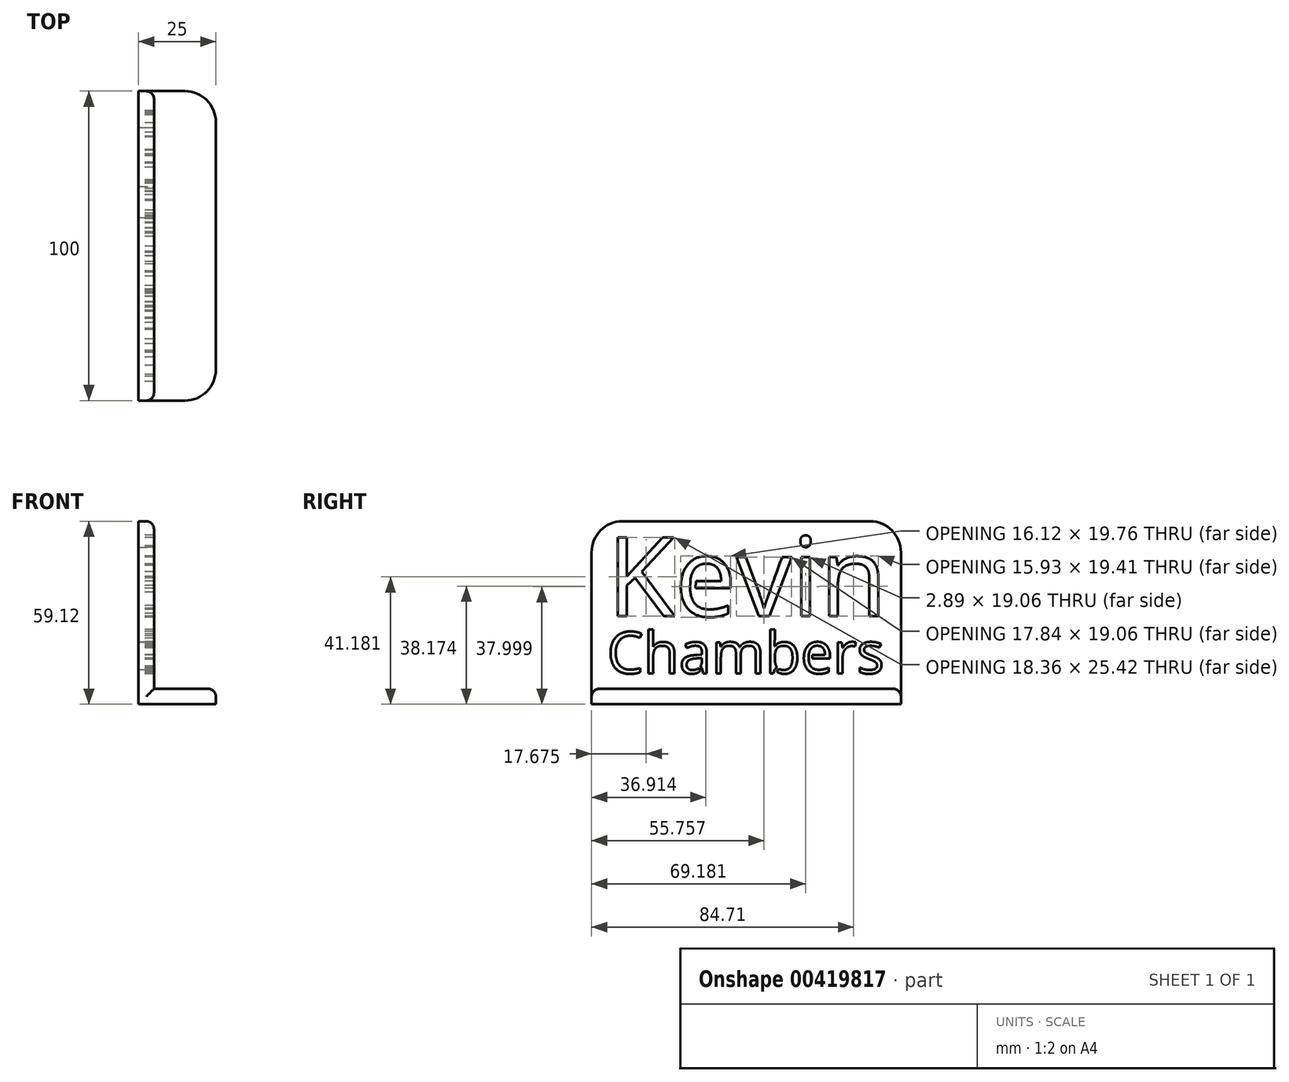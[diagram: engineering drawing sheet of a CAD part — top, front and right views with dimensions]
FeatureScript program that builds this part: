
annotation { "Feature Type Name" : "Feature", "Feature Type Description" : "" }
export const myFeature = defineFeature(function(context is Context, id is Id, definition is map)
    precondition{}
    {
        {
            var Q0;
            Q0=qCreatedBy(makeId("Right.planeOp"),FACE);
            var sketch = newSketch(context, id + "F0", { "sketchPlane" : qUnion([Q0])});
            skLineSegment(sketch, "E0.bottom", {"start": v(0, 0) * mm, "end": v(100, 0) * mm});
            skLineSegment(sketch, "E0.top", {"start": v(0, 54.12) * mm, "end": v(100, 54.12) * mm});
            skLineSegment(sketch, "E0.left", {"start": v(0, 0) * mm, "end": v(0, 54.12) * mm});
            skLineSegment(sketch, "E0.right", {"start": v(100, 0) * mm, "end": v(100, 54.12) * mm});
            skText(sketch, "E1", { "text": "Kevin", "fontName": "OpenSans-Regular.ttf"});
            skText(sketch, "E2", { "text": "Chambers", "fontName": "OpenSans-Regular.ttf"});
            skLineSegment(sketch, "E3", {"start": v(31.97, 34.9) * mm, "end": v(31.85, 32.46) * mm});
            skLineSegment(sketch, "E4", {"start": v(31.85, 32.46) * mm, "end": v(33.67, 32.46) * mm});
            skLineSegment(sketch, "E5", {"start": v(33.67, 32.46) * mm, "end": v(33.71, 34.86) * mm});
            skLineSegment(sketch, "E6", {"start": v(33.71, 34.86) * mm, "end": v(31.97, 34.9) * mm});
            skLineSegment(sketch, "E7", {"start": v(59.2, 6.23) * mm, "end": v(59.89, 7.12) * mm});
            skLineSegment(sketch, "E8", {"start": v(59.89, 7.12) * mm, "end": v(60.67, 6.52) * mm});
            skLineSegment(sketch, "E9", {"start": v(60.67, 6.52) * mm, "end": v(59.78, 5.36) * mm});
            skLineSegment(sketch, "E10", {"start": v(59.78, 5.36) * mm, "end": v(59.2, 6.23) * mm});
            skLineSegment(sketch, "E11", {"start": v(35.74, 6.23) * mm, "end": v(35.23, 7.33) * mm});
            skLineSegment(sketch, "E12", {"start": v(35.23, 7.33) * mm, "end": v(34.64, 6.8) * mm});
            skLineSegment(sketch, "E13", {"start": v(34.64, 6.8) * mm, "end": v(35.27, 5.44) * mm});
            skLineSegment(sketch, "E14", {"start": v(35.27, 5.44) * mm, "end": v(35.74, 6.23) * mm});
            skLineSegment(sketch, "E15", {"start": v(70.25, 9.58) * mm, "end": v(70.25, 11.07) * mm});
            skLineSegment(sketch, "E16", {"start": v(70.25, 11.07) * mm, "end": v(71.3, 11.07) * mm});
            skLineSegment(sketch, "E17", {"start": v(71.3, 11.07) * mm, "end": v(71.3, 9.2) * mm});
            skLineSegment(sketch, "E18", {"start": v(71.3, 9.2) * mm, "end": v(70.25, 9.58) * mm});
            const initialGuessF0  = {"E1": [0.005, 0.02347, 1, 0, 0.02564], "E2": [0.005, 0.005, 1, 0, 0.01347]};
            skSetInitialGuess(sketch, initialGuessF0);
            skSolve(sketch);
        }
        {
            var Q0;
            Q0=makeQuery(id+"F0.imprint","IMPRINT",FACE,{"disambiguationData":[TD([[makeQuery(id+"F0.imprint","IMPRINT",EDGE,{"derivedFrom":sQuery(id+"F0.wireOp",EDGE,"E2.sketch_text.stroke-103")}),1.0]])]});
            var Q1;
            Q1=makeQuery(id+"F0.imprint","IMPRINT",FACE,{"disambiguationData":[TD([[makeQuery(id+"F0.imprint","IMPRINT",EDGE,{"derivedFrom":sQuery(id+"F0.wireOp",EDGE,"E2.sketch_text.stroke-125")}),1.0]])]});
            var Q2;
            {var subQ0=sQuery(id+"F0.wireOp",EDGE,"E17");var subQ1=sQuery(id+"F0.wireOp",EDGE,"E2.sketch_text.stroke-118");var subQ2=makeQuery(id+"F0.imprint","INTERSECT",VERTEX,{"derivedFrom":[subQ1,subQ0]});Q2=makeQuery(id+"F0.imprint","IMPRINT",FACE,{"disambiguationData":[TD([[makeQuery(id+"F0.imprint","IMPRINT",EDGE,{"disambiguationData":[TD([[subQ2,-1.0]])],"derivedFrom":subQ1}),-1.0]])]});}
            var Q3;
            Q3=makeQuery(id+"F0.imprint","IMPRINT",FACE,{"disambiguationData":[TD([[makeQuery(id+"F0.imprint","IMPRINT",EDGE,{"derivedFrom":sQuery(id+"F0.wireOp",EDGE,"E0.bottom")}),1.0]])]});
            var Q4;
            {var subQ1=sQuery(id+"F0.wireOp",EDGE,"E2.sketch_text.stroke-93");var subQ7=sQuery(id+"F0.wireOp",EDGE,"E9");var subQ9=makeQuery(id+"F0.imprint","INTERSECT",VERTEX,{"derivedFrom":[subQ1,subQ7]});Q4=makeQuery(id+"F0.imprint","IMPRINT",FACE,{"disambiguationData":[TD([[makeQuery(id+"F0.imprint","IMPRINT",EDGE,{"disambiguationData":[TD([[subQ9,-1.0]])],"derivedFrom":subQ1}),-1.0]])]});}
            var Q5;
            {var subQ5=sQuery(id+"F0.wireOp",EDGE,"E18");Q5=makeQuery(id+"F0.imprint","IMPRINT",FACE,{"disambiguationData":[TD([[makeQuery(id+"F0.imprint","IMPRINT",EDGE,{"derivedFrom":subQ5}),-1.0]])]});}
            var Q6;
            {var subQ5=sQuery(id+"F0.wireOp",EDGE,"E16");Q6=makeQuery(id+"F0.imprint","IMPRINT",FACE,{"disambiguationData":[TD([[makeQuery(id+"F0.imprint","IMPRINT",EDGE,{"derivedFrom":subQ5}),-1.0]])]});}
            var Q7;
            {var subQ5=sQuery(id+"F0.wireOp",EDGE,"E10");Q7=makeQuery(id+"F0.imprint","IMPRINT",FACE,{"disambiguationData":[TD([[makeQuery(id+"F0.imprint","IMPRINT",EDGE,{"derivedFrom":subQ5}),-1.0]])]});}
            var Q8;
            {var subQ0=sQuery(id+"F0.wireOp",EDGE,"E8");Q8=makeQuery(id+"F0.imprint","IMPRINT",FACE,{"disambiguationData":[TD([[makeQuery(id+"F0.imprint","IMPRINT",EDGE,{"derivedFrom":subQ0}),-1.0]])]});}
            var Q9;
            {var subQ8=sQuery(id+"F0.wireOp",EDGE,"E2.sketch_text.stroke-54");Q9=makeQuery(id+"F0.imprint","IMPRINT",FACE,{"disambiguationData":[TD([[makeQuery(id+"F0.imprint","IMPRINT",EDGE,{"derivedFrom":subQ8}),1.0]])]});}
            var Q10;
            {var subQ0=sQuery(id+"F0.wireOp",EDGE,"E11");var subQ1=sQuery(id+"F0.wireOp",EDGE,"E2.sketch_text.stroke-35");var subQ2=makeQuery(id+"F0.imprint","INTERSECT",VERTEX,{"derivedFrom":[subQ1,subQ0]});Q10=makeQuery(id+"F0.imprint","IMPRINT",FACE,{"disambiguationData":[TD([[makeQuery(id+"F0.imprint","IMPRINT",EDGE,{"disambiguationData":[TD([[subQ2,-1.0]])],"derivedFrom":subQ1}),-1.0]])]});}
            var Q11;
            {var subQ5=sQuery(id+"F0.wireOp",EDGE,"E14");Q11=makeQuery(id+"F0.imprint","IMPRINT",FACE,{"disambiguationData":[TD([[makeQuery(id+"F0.imprint","IMPRINT",EDGE,{"derivedFrom":subQ5}),1.0]])]});}
            var Q12;
            {var subQ0=sQuery(id+"F0.wireOp",EDGE,"E12");Q12=makeQuery(id+"F0.imprint","IMPRINT",FACE,{"disambiguationData":[TD([[makeQuery(id+"F0.imprint","IMPRINT",EDGE,{"derivedFrom":subQ0}),1.0]])]});}
            var Q13;
            {var subQ0=sQuery(id+"F0.wireOp",EDGE,"E5");var subQ1=sQuery(id+"F0.wireOp",EDGE,"E1.sketch_text.stroke-19");var subQ2=makeQuery(id+"F0.imprint","INTERSECT",VERTEX,{"derivedFrom":[subQ1,subQ0]});Q13=makeQuery(id+"F0.imprint","IMPRINT",FACE,{"disambiguationData":[TD([[makeQuery(id+"F0.imprint","IMPRINT",EDGE,{"disambiguationData":[TD([[subQ2,-1.0]])],"derivedFrom":subQ1}),-1.0]])]});}
            var Q14;
            Q14=makeQuery(id+"F0.imprint","IMPRINT",FACE,{"disambiguationData":[TD([[makeQuery(id+"F0.imprint","IMPRINT",EDGE,{"derivedFrom":sQuery(id+"F0.wireOp",EDGE,"E1.sketch_text.stroke-26")}),1.0]])]});
            var Q15;
            {var subQ5=sQuery(id+"F0.wireOp",EDGE,"E6");Q15=makeQuery(id+"F0.imprint","IMPRINT",FACE,{"disambiguationData":[TD([[makeQuery(id+"F0.imprint","IMPRINT",EDGE,{"derivedFrom":subQ5}),1.0]])]});}
            var Q16;
            {var subQ5=sQuery(id+"F0.wireOp",EDGE,"E4");Q16=makeQuery(id+"F0.imprint","IMPRINT",FACE,{"disambiguationData":[TD([[makeQuery(id+"F0.imprint","IMPRINT",EDGE,{"derivedFrom":subQ5}),1.0]])]});}
            extrude(context, id + "F1", {"entities" : qUnion([Q0, Q1, Q2, Q3, Q4, Q5, Q6, Q7, Q8, Q9, Q10, Q11, Q12, Q13, Q14, Q15, Q16]), "depth" : 5 * mm});
        }
        {
            var Q0;
            Q0=makeQuery(id+"F1.opExtrude","SWEPT_EDGE",EDGE,{"disambiguationData":[OSD([sQuery(id+"F0.wireOp",EDGE,"E0.top"),sQuery(id+"F0.wireOp",EDGE,"E0.right")])]});
            var Q1;
            Q1=makeQuery(id+"F1.opExtrude","SWEPT_EDGE",EDGE,{"disambiguationData":[OSD([sQuery(id+"F0.wireOp",EDGE,"E0.top"),sQuery(id+"F0.wireOp",EDGE,"E0.left")])]});
            fillet(context, id + "F2", {"entities" : qUnion([Q0, Q1]), "radius" : 10 * mm, "tangentPropagation" : true, "allowEdgeOverflow" : false});
        }
        {
            var Q0;
            Q0=makeQuery(id+"F1.opExtrude","SWEPT_FACE",FACE,{"disambiguationData":[OSD([sQuery(id+"F0.wireOp",EDGE,"E0.bottom")])]});
            var sketch = newSketch(context, id + "F3", { "sketchPlane" : qUnion([Q0])});
            skLineSegment(sketch, "E19.bottom", {"start": v(0, 0) * mm, "end": v(25, 0) * mm});
            skLineSegment(sketch, "E19.top", {"start": v(0, -100) * mm, "end": v(25, -100) * mm});
            skLineSegment(sketch, "E19.left", {"start": v(0, 0) * mm, "end": v(0, -100) * mm});
            skLineSegment(sketch, "E19.right", {"start": v(25, 0) * mm, "end": v(25, -100) * mm});
            skSolve(sketch);
        }
        {
            var Q0;
            Q0 = qSketchRegion(id + "F3", true);
            extrude(context, id + "F4", {"entities" : qUnion([Q0]), "operationType" : NewBodyOperationType.ADD, "depth" : 5 * mm});
        }
        {
            var Q0;
            Q0=makeQuery(id+"F4.opExtrude","SWEPT_EDGE",EDGE,{"disambiguationData":[OSD([sQuery(id+"F3.wireOp",EDGE,"E19.bottom"),sQuery(id+"F3.wireOp",EDGE,"E19.right")])]});
            var Q1;
            Q1=makeQuery(id+"F4.opExtrude","SWEPT_EDGE",EDGE,{"disambiguationData":[OSD([sQuery(id+"F3.wireOp",EDGE,"E19.top"),sQuery(id+"F3.wireOp",EDGE,"E19.right")])]});
            fillet(context, id + "F5", {"entities" : qUnion([Q0, Q1]), "radius" : 10 * mm, "tangentPropagation" : true, "allowEdgeOverflow" : false});
        }
        {
            var Q0;
            {var subQ0=sQuery(id+"F0.wireOp",EDGE,"E0.left");var subQ1=sQuery(id+"F0.wireOp",EDGE,"E0.top");Q0=makeQuery(id+"F2.opFillet","BLEND_EDGE",EDGE,{"blendedFrom":[makeQuery(id+"F1.opExtrude","SWEPT_EDGE",EDGE,{"disambiguationData":[OSD([subQ1,subQ0])]}),makeQuery(id+"F1.opExtrude","CAP_FACE",FACE,{"disambiguationData":[OSD([sQuery(id+"F0.wireOp",EDGE,"E0.bottom"),subQ1,subQ0,sQuery(id+"F0.wireOp",EDGE,"E0.right"),sQuery(id+"F0.wireOp",EDGE,"E1.sketch_text.stroke-0"),sQuery(id+"F0.wireOp",EDGE,"E1.sketch_text.stroke-1"),sQuery(id+"F0.wireOp",EDGE,"E1.sketch_text.stroke-2"),sQuery(id+"F0.wireOp",EDGE,"E1.sketch_text.stroke-3"),sQuery(id+"F0.wireOp",EDGE,"E1.sketch_text.stroke-4"),sQuery(id+"F0.wireOp",EDGE,"E1.sketch_text.stroke-5"),sQuery(id+"F0.wireOp",EDGE,"E1.sketch_text.stroke-6"),sQuery(id+"F0.wireOp",EDGE,"E1.sketch_text.stroke-7"),sQuery(id+"F0.wireOp",EDGE,"E1.sketch_text.stroke-8"),sQuery(id+"F0.wireOp",EDGE,"E1.sketch_text.stroke-9"),sQuery(id+"F0.wireOp",EDGE,"E1.sketch_text.stroke-10"),sQuery(id+"F0.wireOp",EDGE,"E1.sketch_text.stroke-11"),sQuery(id+"F0.wireOp",EDGE,"E1.sketch_text.stroke-12"),sQuery(id+"F0.wireOp",EDGE,"E1.sketch_text.stroke-13"),sQuery(id+"F0.wireOp",EDGE,"E1.sketch_text.stroke-14"),sQuery(id+"F0.wireOp",EDGE,"E1.sketch_text.stroke-15"),sQuery(id+"F0.wireOp",EDGE,"E1.sketch_text.stroke-16"),sQuery(id+"F0.wireOp",EDGE,"E1.sketch_text.stroke-17"),sQuery(id+"F0.wireOp",EDGE,"E1.sketch_text.stroke-18"),sQuery(id+"F0.wireOp",EDGE,"E1.sketch_text.stroke-19"),sQuery(id+"F0.wireOp",EDGE,"E1.sketch_text.stroke-20"),sQuery(id+"F0.wireOp",EDGE,"E1.sketch_text.stroke-21"),sQuery(id+"F0.wireOp",EDGE,"E1.sketch_text.stroke-22"),sQuery(id+"F0.wireOp",EDGE,"E1.sketch_text.stroke-23"),sQuery(id+"F0.wireOp",EDGE,"E1.sketch_text.stroke-24"),sQuery(id+"F0.wireOp",EDGE,"E1.sketch_text.stroke-25"),sQuery(id+"F0.wireOp",EDGE,"E1.sketch_text.stroke-26"),sQuery(id+"F0.wireOp",EDGE,"E1.sketch_text.stroke-27"),sQuery(id+"F0.wireOp",EDGE,"E1.sketch_text.stroke-28"),sQuery(id+"F0.wireOp",EDGE,"E1.sketch_text.stroke-29"),sQuery(id+"F0.wireOp",EDGE,"E1.sketch_text.stroke-30"),sQuery(id+"F0.wireOp",EDGE,"E1.sketch_text.stroke-31"),sQuery(id+"F0.wireOp",EDGE,"E1.sketch_text.stroke-32"),sQuery(id+"F0.wireOp",EDGE,"E1.sketch_text.stroke-33"),sQuery(id+"F0.wireOp",EDGE,"E1.sketch_text.stroke-34"),sQuery(id+"F0.wireOp",EDGE,"E1.sketch_text.stroke-35"),sQuery(id+"F0.wireOp",EDGE,"E1.sketch_text.stroke-36"),sQuery(id+"F0.wireOp",EDGE,"E1.sketch_text.stroke-37"),sQuery(id+"F0.wireOp",EDGE,"E1.sketch_text.stroke-38"),sQuery(id+"F0.wireOp",EDGE,"E1.sketch_text.stroke-39"),sQuery(id+"F0.wireOp",EDGE,"E1.sketch_text.stroke-40"),sQuery(id+"F0.wireOp",EDGE,"E1.sketch_text.stroke-41"),sQuery(id+"F0.wireOp",EDGE,"E1.sketch_text.stroke-42"),sQuery(id+"F0.wireOp",EDGE,"E1.sketch_text.stroke-43"),sQuery(id+"F0.wireOp",EDGE,"E1.sketch_text.stroke-44"),sQuery(id+"F0.wireOp",EDGE,"E1.sketch_text.stroke-45"),sQuery(id+"F0.wireOp",EDGE,"E1.sketch_text.stroke-46"),sQuery(id+"F0.wireOp",EDGE,"E1.sketch_text.stroke-47"),sQuery(id+"F0.wireOp",EDGE,"E1.sketch_text.stroke-48"),sQuery(id+"F0.wireOp",EDGE,"E1.sketch_text.stroke-49"),sQuery(id+"F0.wireOp",EDGE,"E1.sketch_text.stroke-50"),sQuery(id+"F0.wireOp",EDGE,"E1.sketch_text.stroke-51"),sQuery(id+"F0.wireOp",EDGE,"E1.sketch_text.stroke-52"),sQuery(id+"F0.wireOp",EDGE,"E1.sketch_text.stroke-53"),sQuery(id+"F0.wireOp",EDGE,"E1.sketch_text.stroke-54"),sQuery(id+"F0.wireOp",EDGE,"E1.sketch_text.stroke-55"),sQuery(id+"F0.wireOp",EDGE,"E1.sketch_text.stroke-56"),sQuery(id+"F0.wireOp",EDGE,"E1.sketch_text.stroke-57"),sQuery(id+"F0.wireOp",EDGE,"E1.sketch_text.stroke-58"),sQuery(id+"F0.wireOp",EDGE,"E1.sketch_text.stroke-59"),sQuery(id+"F0.wireOp",EDGE,"E1.sketch_text.stroke-60"),sQuery(id+"F0.wireOp",EDGE,"E1.sketch_text.stroke-61"),sQuery(id+"F0.wireOp",EDGE,"E1.sketch_text.stroke-62"),sQuery(id+"F0.wireOp",EDGE,"E1.sketch_text.stroke-63"),sQuery(id+"F0.wireOp",EDGE,"E1.sketch_text.stroke-64"),sQuery(id+"F0.wireOp",EDGE,"E1.sketch_text.stroke-65"),sQuery(id+"F0.wireOp",EDGE,"E1.sketch_text.stroke-66"),sQuery(id+"F0.wireOp",EDGE,"E1.sketch_text.stroke-67"),sQuery(id+"F0.wireOp",EDGE,"E1.sketch_text.stroke-68"),sQuery(id+"F0.wireOp",EDGE,"E1.sketch_text.stroke-69"),sQuery(id+"F0.wireOp",EDGE,"E2.sketch_text.stroke-0"),sQuery(id+"F0.wireOp",EDGE,"E2.sketch_text.stroke-1"),sQuery(id+"F0.wireOp",EDGE,"E2.sketch_text.stroke-2"),sQuery(id+"F0.wireOp",EDGE,"E2.sketch_text.stroke-3"),sQuery(id+"F0.wireOp",EDGE,"E2.sketch_text.stroke-4"),sQuery(id+"F0.wireOp",EDGE,"E2.sketch_text.stroke-5"),sQuery(id+"F0.wireOp",EDGE,"E2.sketch_text.stroke-6"),sQuery(id+"F0.wireOp",EDGE,"E2.sketch_text.stroke-7"),sQuery(id+"F0.wireOp",EDGE,"E2.sketch_text.stroke-8"),sQuery(id+"F0.wireOp",EDGE,"E2.sketch_text.stroke-9"),sQuery(id+"F0.wireOp",EDGE,"E2.sketch_text.stroke-10"),sQuery(id+"F0.wireOp",EDGE,"E2.sketch_text.stroke-11"),sQuery(id+"F0.wireOp",EDGE,"E2.sketch_text.stroke-12"),sQuery(id+"F0.wireOp",EDGE,"E2.sketch_text.stroke-13"),sQuery(id+"F0.wireOp",EDGE,"E2.sketch_text.stroke-14"),sQuery(id+"F0.wireOp",EDGE,"E2.sketch_text.stroke-15"),sQuery(id+"F0.wireOp",EDGE,"E2.sketch_text.stroke-16"),sQuery(id+"F0.wireOp",EDGE,"E2.sketch_text.stroke-17"),sQuery(id+"F0.wireOp",EDGE,"E2.sketch_text.stroke-18"),sQuery(id+"F0.wireOp",EDGE,"E2.sketch_text.stroke-19"),sQuery(id+"F0.wireOp",EDGE,"E2.sketch_text.stroke-20"),sQuery(id+"F0.wireOp",EDGE,"E2.sketch_text.stroke-21"),sQuery(id+"F0.wireOp",EDGE,"E2.sketch_text.stroke-22"),sQuery(id+"F0.wireOp",EDGE,"E2.sketch_text.stroke-23"),sQuery(id+"F0.wireOp",EDGE,"E2.sketch_text.stroke-24"),sQuery(id+"F0.wireOp",EDGE,"E2.sketch_text.stroke-25"),sQuery(id+"F0.wireOp",EDGE,"E2.sketch_text.stroke-26"),sQuery(id+"F0.wireOp",EDGE,"E2.sketch_text.stroke-27"),sQuery(id+"F0.wireOp",EDGE,"E2.sketch_text.stroke-28"),sQuery(id+"F0.wireOp",EDGE,"E2.sketch_text.stroke-29"),sQuery(id+"F0.wireOp",EDGE,"E2.sketch_text.stroke-30"),sQuery(id+"F0.wireOp",EDGE,"E2.sketch_text.stroke-31"),sQuery(id+"F0.wireOp",EDGE,"E2.sketch_text.stroke-32"),sQuery(id+"F0.wireOp",EDGE,"E2.sketch_text.stroke-33"),sQuery(id+"F0.wireOp",EDGE,"E2.sketch_text.stroke-34"),sQuery(id+"F0.wireOp",EDGE,"E2.sketch_text.stroke-35"),sQuery(id+"F0.wireOp",EDGE,"E2.sketch_text.stroke-36"),sQuery(id+"F0.wireOp",EDGE,"E2.sketch_text.stroke-37"),sQuery(id+"F0.wireOp",EDGE,"E2.sketch_text.stroke-38"),sQuery(id+"F0.wireOp",EDGE,"E2.sketch_text.stroke-39"),sQuery(id+"F0.wireOp",EDGE,"E2.sketch_text.stroke-40"),sQuery(id+"F0.wireOp",EDGE,"E2.sketch_text.stroke-41"),sQuery(id+"F0.wireOp",EDGE,"E2.sketch_text.stroke-42"),sQuery(id+"F0.wireOp",EDGE,"E2.sketch_text.stroke-43"),sQuery(id+"F0.wireOp",EDGE,"E2.sketch_text.stroke-44"),sQuery(id+"F0.wireOp",EDGE,"E2.sketch_text.stroke-45"),sQuery(id+"F0.wireOp",EDGE,"E2.sketch_text.stroke-46"),sQuery(id+"F0.wireOp",EDGE,"E2.sketch_text.stroke-47"),sQuery(id+"F0.wireOp",EDGE,"E2.sketch_text.stroke-48"),sQuery(id+"F0.wireOp",EDGE,"E2.sketch_text.stroke-49"),sQuery(id+"F0.wireOp",EDGE,"E2.sketch_text.stroke-50"),sQuery(id+"F0.wireOp",EDGE,"E2.sketch_text.stroke-51"),sQuery(id+"F0.wireOp",EDGE,"E2.sketch_text.stroke-52"),sQuery(id+"F0.wireOp",EDGE,"E2.sketch_text.stroke-53"),sQuery(id+"F0.wireOp",EDGE,"E2.sketch_text.stroke-54"),sQuery(id+"F0.wireOp",EDGE,"E2.sketch_text.stroke-55"),sQuery(id+"F0.wireOp",EDGE,"E2.sketch_text.stroke-56"),sQuery(id+"F0.wireOp",EDGE,"E2.sketch_text.stroke-57"),sQuery(id+"F0.wireOp",EDGE,"E2.sketch_text.stroke-58"),sQuery(id+"F0.wireOp",EDGE,"E2.sketch_text.stroke-59"),sQuery(id+"F0.wireOp",EDGE,"E2.sketch_text.stroke-60"),sQuery(id+"F0.wireOp",EDGE,"E2.sketch_text.stroke-61"),sQuery(id+"F0.wireOp",EDGE,"E2.sketch_text.stroke-62"),sQuery(id+"F0.wireOp",EDGE,"E2.sketch_text.stroke-63"),sQuery(id+"F0.wireOp",EDGE,"E2.sketch_text.stroke-64"),sQuery(id+"F0.wireOp",EDGE,"E2.sketch_text.stroke-65"),sQuery(id+"F0.wireOp",EDGE,"E2.sketch_text.stroke-66"),sQuery(id+"F0.wireOp",EDGE,"E2.sketch_text.stroke-67"),sQuery(id+"F0.wireOp",EDGE,"E2.sketch_text.stroke-68"),sQuery(id+"F0.wireOp",EDGE,"E2.sketch_text.stroke-69"),sQuery(id+"F0.wireOp",EDGE,"E2.sketch_text.stroke-70"),sQuery(id+"F0.wireOp",EDGE,"E2.sketch_text.stroke-71"),sQuery(id+"F0.wireOp",EDGE,"E2.sketch_text.stroke-72"),sQuery(id+"F0.wireOp",EDGE,"E2.sketch_text.stroke-73"),sQuery(id+"F0.wireOp",EDGE,"E2.sketch_text.stroke-74"),sQuery(id+"F0.wireOp",EDGE,"E2.sketch_text.stroke-75"),sQuery(id+"F0.wireOp",EDGE,"E2.sketch_text.stroke-76"),sQuery(id+"F0.wireOp",EDGE,"E2.sketch_text.stroke-77"),sQuery(id+"F0.wireOp",EDGE,"E2.sketch_text.stroke-78"),sQuery(id+"F0.wireOp",EDGE,"E2.sketch_text.stroke-79"),sQuery(id+"F0.wireOp",EDGE,"E2.sketch_text.stroke-80"),sQuery(id+"F0.wireOp",EDGE,"E2.sketch_text.stroke-81"),sQuery(id+"F0.wireOp",EDGE,"E2.sketch_text.stroke-82"),sQuery(id+"F0.wireOp",EDGE,"E2.sketch_text.stroke-83"),sQuery(id+"F0.wireOp",EDGE,"E2.sketch_text.stroke-84"),sQuery(id+"F0.wireOp",EDGE,"E2.sketch_text.stroke-85"),sQuery(id+"F0.wireOp",EDGE,"E2.sketch_text.stroke-86"),sQuery(id+"F0.wireOp",EDGE,"E2.sketch_text.stroke-87"),sQuery(id+"F0.wireOp",EDGE,"E2.sketch_text.stroke-88"),sQuery(id+"F0.wireOp",EDGE,"E2.sketch_text.stroke-89"),sQuery(id+"F0.wireOp",EDGE,"E2.sketch_text.stroke-90"),sQuery(id+"F0.wireOp",EDGE,"E2.sketch_text.stroke-91"),sQuery(id+"F0.wireOp",EDGE,"E2.sketch_text.stroke-92"),sQuery(id+"F0.wireOp",EDGE,"E2.sketch_text.stroke-93"),sQuery(id+"F0.wireOp",EDGE,"E2.sketch_text.stroke-94"),sQuery(id+"F0.wireOp",EDGE,"E2.sketch_text.stroke-95"),sQuery(id+"F0.wireOp",EDGE,"E2.sketch_text.stroke-96"),sQuery(id+"F0.wireOp",EDGE,"E2.sketch_text.stroke-97"),sQuery(id+"F0.wireOp",EDGE,"E2.sketch_text.stroke-98"),sQuery(id+"F0.wireOp",EDGE,"E2.sketch_text.stroke-99"),sQuery(id+"F0.wireOp",EDGE,"E2.sketch_text.stroke-100"),sQuery(id+"F0.wireOp",EDGE,"E2.sketch_text.stroke-101"),sQuery(id+"F0.wireOp",EDGE,"E2.sketch_text.stroke-102"),sQuery(id+"F0.wireOp",EDGE,"E2.sketch_text.stroke-103"),sQuery(id+"F0.wireOp",EDGE,"E2.sketch_text.stroke-104"),sQuery(id+"F0.wireOp",EDGE,"E2.sketch_text.stroke-105"),sQuery(id+"F0.wireOp",EDGE,"E2.sketch_text.stroke-106"),sQuery(id+"F0.wireOp",EDGE,"E2.sketch_text.stroke-107"),sQuery(id+"F0.wireOp",EDGE,"E2.sketch_text.stroke-108"),sQuery(id+"F0.wireOp",EDGE,"E2.sketch_text.stroke-109"),sQuery(id+"F0.wireOp",EDGE,"E2.sketch_text.stroke-110"),sQuery(id+"F0.wireOp",EDGE,"E2.sketch_text.stroke-111"),sQuery(id+"F0.wireOp",EDGE,"E2.sketch_text.stroke-112"),sQuery(id+"F0.wireOp",EDGE,"E2.sketch_text.stroke-113"),sQuery(id+"F0.wireOp",EDGE,"E2.sketch_text.stroke-114"),sQuery(id+"F0.wireOp",EDGE,"E2.sketch_text.stroke-115"),sQuery(id+"F0.wireOp",EDGE,"E2.sketch_text.stroke-116"),sQuery(id+"F0.wireOp",EDGE,"E2.sketch_text.stroke-117"),sQuery(id+"F0.wireOp",EDGE,"E2.sketch_text.stroke-118"),sQuery(id+"F0.wireOp",EDGE,"E2.sketch_text.stroke-119"),sQuery(id+"F0.wireOp",EDGE,"E2.sketch_text.stroke-120"),sQuery(id+"F0.wireOp",EDGE,"E2.sketch_text.stroke-121"),sQuery(id+"F0.wireOp",EDGE,"E2.sketch_text.stroke-122"),sQuery(id+"F0.wireOp",EDGE,"E2.sketch_text.stroke-123"),sQuery(id+"F0.wireOp",EDGE,"E2.sketch_text.stroke-124"),sQuery(id+"F0.wireOp",EDGE,"E2.sketch_text.stroke-125"),sQuery(id+"F0.wireOp",EDGE,"E2.sketch_text.stroke-126"),sQuery(id+"F0.wireOp",EDGE,"E2.sketch_text.stroke-127"),sQuery(id+"F0.wireOp",EDGE,"E2.sketch_text.stroke-128"),sQuery(id+"F0.wireOp",EDGE,"E2.sketch_text.stroke-129"),sQuery(id+"F0.wireOp",EDGE,"E2.sketch_text.stroke-130"),sQuery(id+"F0.wireOp",EDGE,"E2.sketch_text.stroke-131"),sQuery(id+"F0.wireOp",EDGE,"E2.sketch_text.stroke-132"),sQuery(id+"F0.wireOp",EDGE,"E2.sketch_text.stroke-133"),sQuery(id+"F0.wireOp",EDGE,"E2.sketch_text.stroke-134"),sQuery(id+"F0.wireOp",EDGE,"E2.sketch_text.stroke-135"),sQuery(id+"F0.wireOp",EDGE,"E2.sketch_text.stroke-136"),sQuery(id+"F0.wireOp",EDGE,"E2.sketch_text.stroke-137"),sQuery(id+"F0.wireOp",EDGE,"E2.sketch_text.stroke-138"),sQuery(id+"F0.wireOp",EDGE,"E2.sketch_text.stroke-139"),sQuery(id+"F0.wireOp",EDGE,"E2.sketch_text.stroke-140"),sQuery(id+"F0.wireOp",EDGE,"E2.sketch_text.stroke-141"),sQuery(id+"F0.wireOp",EDGE,"E2.sketch_text.stroke-142"),sQuery(id+"F0.wireOp",EDGE,"E2.sketch_text.stroke-143"),sQuery(id+"F0.wireOp",EDGE,"E2.sketch_text.stroke-144"),sQuery(id+"F0.wireOp",EDGE,"E2.sketch_text.stroke-145"),sQuery(id+"F0.wireOp",EDGE,"E2.sketch_text.stroke-146"),sQuery(id+"F0.wireOp",EDGE,"E2.sketch_text.stroke-147"),sQuery(id+"F0.wireOp",EDGE,"E2.sketch_text.stroke-148"),sQuery(id+"F0.wireOp",EDGE,"E2.sketch_text.stroke-149"),sQuery(id+"F0.wireOp",EDGE,"E2.sketch_text.stroke-150"),sQuery(id+"F0.wireOp",EDGE,"E2.sketch_text.stroke-151"),sQuery(id+"F0.wireOp",EDGE,"E2.sketch_text.stroke-152"),sQuery(id+"F0.wireOp",EDGE,"E2.sketch_text.stroke-153"),sQuery(id+"F0.wireOp",EDGE,"E2.sketch_text.stroke-154"),sQuery(id+"F0.wireOp",EDGE,"E2.sketch_text.stroke-155"),sQuery(id+"F0.wireOp",EDGE,"E2.sketch_text.stroke-156"),sQuery(id+"F0.wireOp",EDGE,"E2.sketch_text.stroke-157"),sQuery(id+"F0.wireOp",EDGE,"E2.sketch_text.stroke-158"),sQuery(id+"F0.wireOp",EDGE,"E2.sketch_text.stroke-159"),sQuery(id+"F0.wireOp",EDGE,"E2.sketch_text.stroke-160"),sQuery(id+"F0.wireOp",EDGE,"E2.sketch_text.stroke-161"),sQuery(id+"F0.wireOp",EDGE,"E2.sketch_text.stroke-162"),sQuery(id+"F0.wireOp",EDGE,"E2.sketch_text.stroke-163"),sQuery(id+"F0.wireOp",EDGE,"E2.sketch_text.stroke-164"),sQuery(id+"F0.wireOp",EDGE,"E2.sketch_text.stroke-165"),sQuery(id+"F0.wireOp",EDGE,"E2.sketch_text.stroke-166"),sQuery(id+"F0.wireOp",EDGE,"E2.sketch_text.stroke-167"),sQuery(id+"F0.wireOp",EDGE,"E3"),sQuery(id+"F0.wireOp",EDGE,"E5"),sQuery(id+"F0.wireOp",EDGE,"E7"),sQuery(id+"F0.wireOp",EDGE,"E9"),sQuery(id+"F0.wireOp",EDGE,"E11"),sQuery(id+"F0.wireOp",EDGE,"E13"),sQuery(id+"F0.wireOp",EDGE,"E15"),sQuery(id+"F0.wireOp",EDGE,"E17")])],"isStart":false})],"blendedInto":[makeQuery(id+"F1.opExtrude","CAP_FACE",FACE,{"disambiguationData":[OSD([sQuery(id+"F0.wireOp",EDGE,"E0.bottom"),subQ1,subQ0,sQuery(id+"F0.wireOp",EDGE,"E0.right"),sQuery(id+"F0.wireOp",EDGE,"E1.sketch_text.stroke-0"),sQuery(id+"F0.wireOp",EDGE,"E1.sketch_text.stroke-1"),sQuery(id+"F0.wireOp",EDGE,"E1.sketch_text.stroke-2"),sQuery(id+"F0.wireOp",EDGE,"E1.sketch_text.stroke-3"),sQuery(id+"F0.wireOp",EDGE,"E1.sketch_text.stroke-4"),sQuery(id+"F0.wireOp",EDGE,"E1.sketch_text.stroke-5"),sQuery(id+"F0.wireOp",EDGE,"E1.sketch_text.stroke-6"),sQuery(id+"F0.wireOp",EDGE,"E1.sketch_text.stroke-7"),sQuery(id+"F0.wireOp",EDGE,"E1.sketch_text.stroke-8"),sQuery(id+"F0.wireOp",EDGE,"E1.sketch_text.stroke-9"),sQuery(id+"F0.wireOp",EDGE,"E1.sketch_text.stroke-10"),sQuery(id+"F0.wireOp",EDGE,"E1.sketch_text.stroke-11"),sQuery(id+"F0.wireOp",EDGE,"E1.sketch_text.stroke-12"),sQuery(id+"F0.wireOp",EDGE,"E1.sketch_text.stroke-13"),sQuery(id+"F0.wireOp",EDGE,"E1.sketch_text.stroke-14"),sQuery(id+"F0.wireOp",EDGE,"E1.sketch_text.stroke-15"),sQuery(id+"F0.wireOp",EDGE,"E1.sketch_text.stroke-16"),sQuery(id+"F0.wireOp",EDGE,"E1.sketch_text.stroke-17"),sQuery(id+"F0.wireOp",EDGE,"E1.sketch_text.stroke-18"),sQuery(id+"F0.wireOp",EDGE,"E1.sketch_text.stroke-19"),sQuery(id+"F0.wireOp",EDGE,"E1.sketch_text.stroke-20"),sQuery(id+"F0.wireOp",EDGE,"E1.sketch_text.stroke-21"),sQuery(id+"F0.wireOp",EDGE,"E1.sketch_text.stroke-22"),sQuery(id+"F0.wireOp",EDGE,"E1.sketch_text.stroke-23"),sQuery(id+"F0.wireOp",EDGE,"E1.sketch_text.stroke-24"),sQuery(id+"F0.wireOp",EDGE,"E1.sketch_text.stroke-25"),sQuery(id+"F0.wireOp",EDGE,"E1.sketch_text.stroke-26"),sQuery(id+"F0.wireOp",EDGE,"E1.sketch_text.stroke-27"),sQuery(id+"F0.wireOp",EDGE,"E1.sketch_text.stroke-28"),sQuery(id+"F0.wireOp",EDGE,"E1.sketch_text.stroke-29"),sQuery(id+"F0.wireOp",EDGE,"E1.sketch_text.stroke-30"),sQuery(id+"F0.wireOp",EDGE,"E1.sketch_text.stroke-31"),sQuery(id+"F0.wireOp",EDGE,"E1.sketch_text.stroke-32"),sQuery(id+"F0.wireOp",EDGE,"E1.sketch_text.stroke-33"),sQuery(id+"F0.wireOp",EDGE,"E1.sketch_text.stroke-34"),sQuery(id+"F0.wireOp",EDGE,"E1.sketch_text.stroke-35"),sQuery(id+"F0.wireOp",EDGE,"E1.sketch_text.stroke-36"),sQuery(id+"F0.wireOp",EDGE,"E1.sketch_text.stroke-37"),sQuery(id+"F0.wireOp",EDGE,"E1.sketch_text.stroke-38"),sQuery(id+"F0.wireOp",EDGE,"E1.sketch_text.stroke-39"),sQuery(id+"F0.wireOp",EDGE,"E1.sketch_text.stroke-40"),sQuery(id+"F0.wireOp",EDGE,"E1.sketch_text.stroke-41"),sQuery(id+"F0.wireOp",EDGE,"E1.sketch_text.stroke-42"),sQuery(id+"F0.wireOp",EDGE,"E1.sketch_text.stroke-43"),sQuery(id+"F0.wireOp",EDGE,"E1.sketch_text.stroke-44"),sQuery(id+"F0.wireOp",EDGE,"E1.sketch_text.stroke-45"),sQuery(id+"F0.wireOp",EDGE,"E1.sketch_text.stroke-46"),sQuery(id+"F0.wireOp",EDGE,"E1.sketch_text.stroke-47"),sQuery(id+"F0.wireOp",EDGE,"E1.sketch_text.stroke-48"),sQuery(id+"F0.wireOp",EDGE,"E1.sketch_text.stroke-49"),sQuery(id+"F0.wireOp",EDGE,"E1.sketch_text.stroke-50"),sQuery(id+"F0.wireOp",EDGE,"E1.sketch_text.stroke-51"),sQuery(id+"F0.wireOp",EDGE,"E1.sketch_text.stroke-52"),sQuery(id+"F0.wireOp",EDGE,"E1.sketch_text.stroke-53"),sQuery(id+"F0.wireOp",EDGE,"E1.sketch_text.stroke-54"),sQuery(id+"F0.wireOp",EDGE,"E1.sketch_text.stroke-55"),sQuery(id+"F0.wireOp",EDGE,"E1.sketch_text.stroke-56"),sQuery(id+"F0.wireOp",EDGE,"E1.sketch_text.stroke-57"),sQuery(id+"F0.wireOp",EDGE,"E1.sketch_text.stroke-58"),sQuery(id+"F0.wireOp",EDGE,"E1.sketch_text.stroke-59"),sQuery(id+"F0.wireOp",EDGE,"E1.sketch_text.stroke-60"),sQuery(id+"F0.wireOp",EDGE,"E1.sketch_text.stroke-61"),sQuery(id+"F0.wireOp",EDGE,"E1.sketch_text.stroke-62"),sQuery(id+"F0.wireOp",EDGE,"E1.sketch_text.stroke-63"),sQuery(id+"F0.wireOp",EDGE,"E1.sketch_text.stroke-64"),sQuery(id+"F0.wireOp",EDGE,"E1.sketch_text.stroke-65"),sQuery(id+"F0.wireOp",EDGE,"E1.sketch_text.stroke-66"),sQuery(id+"F0.wireOp",EDGE,"E1.sketch_text.stroke-67"),sQuery(id+"F0.wireOp",EDGE,"E1.sketch_text.stroke-68"),sQuery(id+"F0.wireOp",EDGE,"E1.sketch_text.stroke-69"),sQuery(id+"F0.wireOp",EDGE,"E2.sketch_text.stroke-0"),sQuery(id+"F0.wireOp",EDGE,"E2.sketch_text.stroke-1"),sQuery(id+"F0.wireOp",EDGE,"E2.sketch_text.stroke-2"),sQuery(id+"F0.wireOp",EDGE,"E2.sketch_text.stroke-3"),sQuery(id+"F0.wireOp",EDGE,"E2.sketch_text.stroke-4"),sQuery(id+"F0.wireOp",EDGE,"E2.sketch_text.stroke-5"),sQuery(id+"F0.wireOp",EDGE,"E2.sketch_text.stroke-6"),sQuery(id+"F0.wireOp",EDGE,"E2.sketch_text.stroke-7"),sQuery(id+"F0.wireOp",EDGE,"E2.sketch_text.stroke-8"),sQuery(id+"F0.wireOp",EDGE,"E2.sketch_text.stroke-9"),sQuery(id+"F0.wireOp",EDGE,"E2.sketch_text.stroke-10"),sQuery(id+"F0.wireOp",EDGE,"E2.sketch_text.stroke-11"),sQuery(id+"F0.wireOp",EDGE,"E2.sketch_text.stroke-12"),sQuery(id+"F0.wireOp",EDGE,"E2.sketch_text.stroke-13"),sQuery(id+"F0.wireOp",EDGE,"E2.sketch_text.stroke-14"),sQuery(id+"F0.wireOp",EDGE,"E2.sketch_text.stroke-15"),sQuery(id+"F0.wireOp",EDGE,"E2.sketch_text.stroke-16"),sQuery(id+"F0.wireOp",EDGE,"E2.sketch_text.stroke-17"),sQuery(id+"F0.wireOp",EDGE,"E2.sketch_text.stroke-18"),sQuery(id+"F0.wireOp",EDGE,"E2.sketch_text.stroke-19"),sQuery(id+"F0.wireOp",EDGE,"E2.sketch_text.stroke-20"),sQuery(id+"F0.wireOp",EDGE,"E2.sketch_text.stroke-21"),sQuery(id+"F0.wireOp",EDGE,"E2.sketch_text.stroke-22"),sQuery(id+"F0.wireOp",EDGE,"E2.sketch_text.stroke-23"),sQuery(id+"F0.wireOp",EDGE,"E2.sketch_text.stroke-24"),sQuery(id+"F0.wireOp",EDGE,"E2.sketch_text.stroke-25"),sQuery(id+"F0.wireOp",EDGE,"E2.sketch_text.stroke-26"),sQuery(id+"F0.wireOp",EDGE,"E2.sketch_text.stroke-27"),sQuery(id+"F0.wireOp",EDGE,"E2.sketch_text.stroke-28"),sQuery(id+"F0.wireOp",EDGE,"E2.sketch_text.stroke-29"),sQuery(id+"F0.wireOp",EDGE,"E2.sketch_text.stroke-30"),sQuery(id+"F0.wireOp",EDGE,"E2.sketch_text.stroke-31"),sQuery(id+"F0.wireOp",EDGE,"E2.sketch_text.stroke-32"),sQuery(id+"F0.wireOp",EDGE,"E2.sketch_text.stroke-33"),sQuery(id+"F0.wireOp",EDGE,"E2.sketch_text.stroke-34"),sQuery(id+"F0.wireOp",EDGE,"E2.sketch_text.stroke-35"),sQuery(id+"F0.wireOp",EDGE,"E2.sketch_text.stroke-36"),sQuery(id+"F0.wireOp",EDGE,"E2.sketch_text.stroke-37"),sQuery(id+"F0.wireOp",EDGE,"E2.sketch_text.stroke-38"),sQuery(id+"F0.wireOp",EDGE,"E2.sketch_text.stroke-39"),sQuery(id+"F0.wireOp",EDGE,"E2.sketch_text.stroke-40"),sQuery(id+"F0.wireOp",EDGE,"E2.sketch_text.stroke-41"),sQuery(id+"F0.wireOp",EDGE,"E2.sketch_text.stroke-42"),sQuery(id+"F0.wireOp",EDGE,"E2.sketch_text.stroke-43"),sQuery(id+"F0.wireOp",EDGE,"E2.sketch_text.stroke-44"),sQuery(id+"F0.wireOp",EDGE,"E2.sketch_text.stroke-45"),sQuery(id+"F0.wireOp",EDGE,"E2.sketch_text.stroke-46"),sQuery(id+"F0.wireOp",EDGE,"E2.sketch_text.stroke-47"),sQuery(id+"F0.wireOp",EDGE,"E2.sketch_text.stroke-48"),sQuery(id+"F0.wireOp",EDGE,"E2.sketch_text.stroke-49"),sQuery(id+"F0.wireOp",EDGE,"E2.sketch_text.stroke-50"),sQuery(id+"F0.wireOp",EDGE,"E2.sketch_text.stroke-51"),sQuery(id+"F0.wireOp",EDGE,"E2.sketch_text.stroke-52"),sQuery(id+"F0.wireOp",EDGE,"E2.sketch_text.stroke-53"),sQuery(id+"F0.wireOp",EDGE,"E2.sketch_text.stroke-54"),sQuery(id+"F0.wireOp",EDGE,"E2.sketch_text.stroke-55"),sQuery(id+"F0.wireOp",EDGE,"E2.sketch_text.stroke-56"),sQuery(id+"F0.wireOp",EDGE,"E2.sketch_text.stroke-57"),sQuery(id+"F0.wireOp",EDGE,"E2.sketch_text.stroke-58"),sQuery(id+"F0.wireOp",EDGE,"E2.sketch_text.stroke-59"),sQuery(id+"F0.wireOp",EDGE,"E2.sketch_text.stroke-60"),sQuery(id+"F0.wireOp",EDGE,"E2.sketch_text.stroke-61"),sQuery(id+"F0.wireOp",EDGE,"E2.sketch_text.stroke-62"),sQuery(id+"F0.wireOp",EDGE,"E2.sketch_text.stroke-63"),sQuery(id+"F0.wireOp",EDGE,"E2.sketch_text.stroke-64"),sQuery(id+"F0.wireOp",EDGE,"E2.sketch_text.stroke-65"),sQuery(id+"F0.wireOp",EDGE,"E2.sketch_text.stroke-66"),sQuery(id+"F0.wireOp",EDGE,"E2.sketch_text.stroke-67"),sQuery(id+"F0.wireOp",EDGE,"E2.sketch_text.stroke-68"),sQuery(id+"F0.wireOp",EDGE,"E2.sketch_text.stroke-69"),sQuery(id+"F0.wireOp",EDGE,"E2.sketch_text.stroke-70"),sQuery(id+"F0.wireOp",EDGE,"E2.sketch_text.stroke-71"),sQuery(id+"F0.wireOp",EDGE,"E2.sketch_text.stroke-72"),sQuery(id+"F0.wireOp",EDGE,"E2.sketch_text.stroke-73"),sQuery(id+"F0.wireOp",EDGE,"E2.sketch_text.stroke-74"),sQuery(id+"F0.wireOp",EDGE,"E2.sketch_text.stroke-75"),sQuery(id+"F0.wireOp",EDGE,"E2.sketch_text.stroke-76"),sQuery(id+"F0.wireOp",EDGE,"E2.sketch_text.stroke-77"),sQuery(id+"F0.wireOp",EDGE,"E2.sketch_text.stroke-78"),sQuery(id+"F0.wireOp",EDGE,"E2.sketch_text.stroke-79"),sQuery(id+"F0.wireOp",EDGE,"E2.sketch_text.stroke-80"),sQuery(id+"F0.wireOp",EDGE,"E2.sketch_text.stroke-81"),sQuery(id+"F0.wireOp",EDGE,"E2.sketch_text.stroke-82"),sQuery(id+"F0.wireOp",EDGE,"E2.sketch_text.stroke-83"),sQuery(id+"F0.wireOp",EDGE,"E2.sketch_text.stroke-84"),sQuery(id+"F0.wireOp",EDGE,"E2.sketch_text.stroke-85"),sQuery(id+"F0.wireOp",EDGE,"E2.sketch_text.stroke-86"),sQuery(id+"F0.wireOp",EDGE,"E2.sketch_text.stroke-87"),sQuery(id+"F0.wireOp",EDGE,"E2.sketch_text.stroke-88"),sQuery(id+"F0.wireOp",EDGE,"E2.sketch_text.stroke-89"),sQuery(id+"F0.wireOp",EDGE,"E2.sketch_text.stroke-90"),sQuery(id+"F0.wireOp",EDGE,"E2.sketch_text.stroke-91"),sQuery(id+"F0.wireOp",EDGE,"E2.sketch_text.stroke-92"),sQuery(id+"F0.wireOp",EDGE,"E2.sketch_text.stroke-93"),sQuery(id+"F0.wireOp",EDGE,"E2.sketch_text.stroke-94"),sQuery(id+"F0.wireOp",EDGE,"E2.sketch_text.stroke-95"),sQuery(id+"F0.wireOp",EDGE,"E2.sketch_text.stroke-96"),sQuery(id+"F0.wireOp",EDGE,"E2.sketch_text.stroke-97"),sQuery(id+"F0.wireOp",EDGE,"E2.sketch_text.stroke-98"),sQuery(id+"F0.wireOp",EDGE,"E2.sketch_text.stroke-99"),sQuery(id+"F0.wireOp",EDGE,"E2.sketch_text.stroke-100"),sQuery(id+"F0.wireOp",EDGE,"E2.sketch_text.stroke-101"),sQuery(id+"F0.wireOp",EDGE,"E2.sketch_text.stroke-102"),sQuery(id+"F0.wireOp",EDGE,"E2.sketch_text.stroke-103"),sQuery(id+"F0.wireOp",EDGE,"E2.sketch_text.stroke-104"),sQuery(id+"F0.wireOp",EDGE,"E2.sketch_text.stroke-105"),sQuery(id+"F0.wireOp",EDGE,"E2.sketch_text.stroke-106"),sQuery(id+"F0.wireOp",EDGE,"E2.sketch_text.stroke-107"),sQuery(id+"F0.wireOp",EDGE,"E2.sketch_text.stroke-108"),sQuery(id+"F0.wireOp",EDGE,"E2.sketch_text.stroke-109"),sQuery(id+"F0.wireOp",EDGE,"E2.sketch_text.stroke-110"),sQuery(id+"F0.wireOp",EDGE,"E2.sketch_text.stroke-111"),sQuery(id+"F0.wireOp",EDGE,"E2.sketch_text.stroke-112"),sQuery(id+"F0.wireOp",EDGE,"E2.sketch_text.stroke-113"),sQuery(id+"F0.wireOp",EDGE,"E2.sketch_text.stroke-114"),sQuery(id+"F0.wireOp",EDGE,"E2.sketch_text.stroke-115"),sQuery(id+"F0.wireOp",EDGE,"E2.sketch_text.stroke-116"),sQuery(id+"F0.wireOp",EDGE,"E2.sketch_text.stroke-117"),sQuery(id+"F0.wireOp",EDGE,"E2.sketch_text.stroke-118"),sQuery(id+"F0.wireOp",EDGE,"E2.sketch_text.stroke-119"),sQuery(id+"F0.wireOp",EDGE,"E2.sketch_text.stroke-120"),sQuery(id+"F0.wireOp",EDGE,"E2.sketch_text.stroke-121"),sQuery(id+"F0.wireOp",EDGE,"E2.sketch_text.stroke-122"),sQuery(id+"F0.wireOp",EDGE,"E2.sketch_text.stroke-123"),sQuery(id+"F0.wireOp",EDGE,"E2.sketch_text.stroke-124"),sQuery(id+"F0.wireOp",EDGE,"E2.sketch_text.stroke-125"),sQuery(id+"F0.wireOp",EDGE,"E2.sketch_text.stroke-126"),sQuery(id+"F0.wireOp",EDGE,"E2.sketch_text.stroke-127"),sQuery(id+"F0.wireOp",EDGE,"E2.sketch_text.stroke-128"),sQuery(id+"F0.wireOp",EDGE,"E2.sketch_text.stroke-129"),sQuery(id+"F0.wireOp",EDGE,"E2.sketch_text.stroke-130"),sQuery(id+"F0.wireOp",EDGE,"E2.sketch_text.stroke-131"),sQuery(id+"F0.wireOp",EDGE,"E2.sketch_text.stroke-132"),sQuery(id+"F0.wireOp",EDGE,"E2.sketch_text.stroke-133"),sQuery(id+"F0.wireOp",EDGE,"E2.sketch_text.stroke-134"),sQuery(id+"F0.wireOp",EDGE,"E2.sketch_text.stroke-135"),sQuery(id+"F0.wireOp",EDGE,"E2.sketch_text.stroke-136"),sQuery(id+"F0.wireOp",EDGE,"E2.sketch_text.stroke-137"),sQuery(id+"F0.wireOp",EDGE,"E2.sketch_text.stroke-138"),sQuery(id+"F0.wireOp",EDGE,"E2.sketch_text.stroke-139"),sQuery(id+"F0.wireOp",EDGE,"E2.sketch_text.stroke-140"),sQuery(id+"F0.wireOp",EDGE,"E2.sketch_text.stroke-141"),sQuery(id+"F0.wireOp",EDGE,"E2.sketch_text.stroke-142"),sQuery(id+"F0.wireOp",EDGE,"E2.sketch_text.stroke-143"),sQuery(id+"F0.wireOp",EDGE,"E2.sketch_text.stroke-144"),sQuery(id+"F0.wireOp",EDGE,"E2.sketch_text.stroke-145"),sQuery(id+"F0.wireOp",EDGE,"E2.sketch_text.stroke-146"),sQuery(id+"F0.wireOp",EDGE,"E2.sketch_text.stroke-147"),sQuery(id+"F0.wireOp",EDGE,"E2.sketch_text.stroke-148"),sQuery(id+"F0.wireOp",EDGE,"E2.sketch_text.stroke-149"),sQuery(id+"F0.wireOp",EDGE,"E2.sketch_text.stroke-150"),sQuery(id+"F0.wireOp",EDGE,"E2.sketch_text.stroke-151"),sQuery(id+"F0.wireOp",EDGE,"E2.sketch_text.stroke-152"),sQuery(id+"F0.wireOp",EDGE,"E2.sketch_text.stroke-153"),sQuery(id+"F0.wireOp",EDGE,"E2.sketch_text.stroke-154"),sQuery(id+"F0.wireOp",EDGE,"E2.sketch_text.stroke-155"),sQuery(id+"F0.wireOp",EDGE,"E2.sketch_text.stroke-156"),sQuery(id+"F0.wireOp",EDGE,"E2.sketch_text.stroke-157"),sQuery(id+"F0.wireOp",EDGE,"E2.sketch_text.stroke-158"),sQuery(id+"F0.wireOp",EDGE,"E2.sketch_text.stroke-159"),sQuery(id+"F0.wireOp",EDGE,"E2.sketch_text.stroke-160"),sQuery(id+"F0.wireOp",EDGE,"E2.sketch_text.stroke-161"),sQuery(id+"F0.wireOp",EDGE,"E2.sketch_text.stroke-162"),sQuery(id+"F0.wireOp",EDGE,"E2.sketch_text.stroke-163"),sQuery(id+"F0.wireOp",EDGE,"E2.sketch_text.stroke-164"),sQuery(id+"F0.wireOp",EDGE,"E2.sketch_text.stroke-165"),sQuery(id+"F0.wireOp",EDGE,"E2.sketch_text.stroke-166"),sQuery(id+"F0.wireOp",EDGE,"E2.sketch_text.stroke-167"),sQuery(id+"F0.wireOp",EDGE,"E3"),sQuery(id+"F0.wireOp",EDGE,"E5"),sQuery(id+"F0.wireOp",EDGE,"E7"),sQuery(id+"F0.wireOp",EDGE,"E9"),sQuery(id+"F0.wireOp",EDGE,"E11"),sQuery(id+"F0.wireOp",EDGE,"E13"),sQuery(id+"F0.wireOp",EDGE,"E15"),sQuery(id+"F0.wireOp",EDGE,"E17")])],"isStart":false})]});}
            var Q1;
            Q1=makeQuery(id+"F4.opExtrude","CAP_EDGE",EDGE,{"disambiguationData":[OSD([sQuery(id+"F3.wireOp",EDGE,"E19.right")])],"isStart":true});
            var Q2;
            Q2=makeQuery(id+"F1.opExtrude","CAP_EDGE",EDGE,{"disambiguationData":[OSD([sQuery(id+"F0.wireOp",EDGE,"E0.bottom")])],"isStart":false});
            fillet(context, id + "F6", {"entities" : qUnion([Q0, Q1, Q2]), "radius" : 2.5 * mm, "tangentPropagation" : true, "allowEdgeOverflow" : false});
        }
    });
